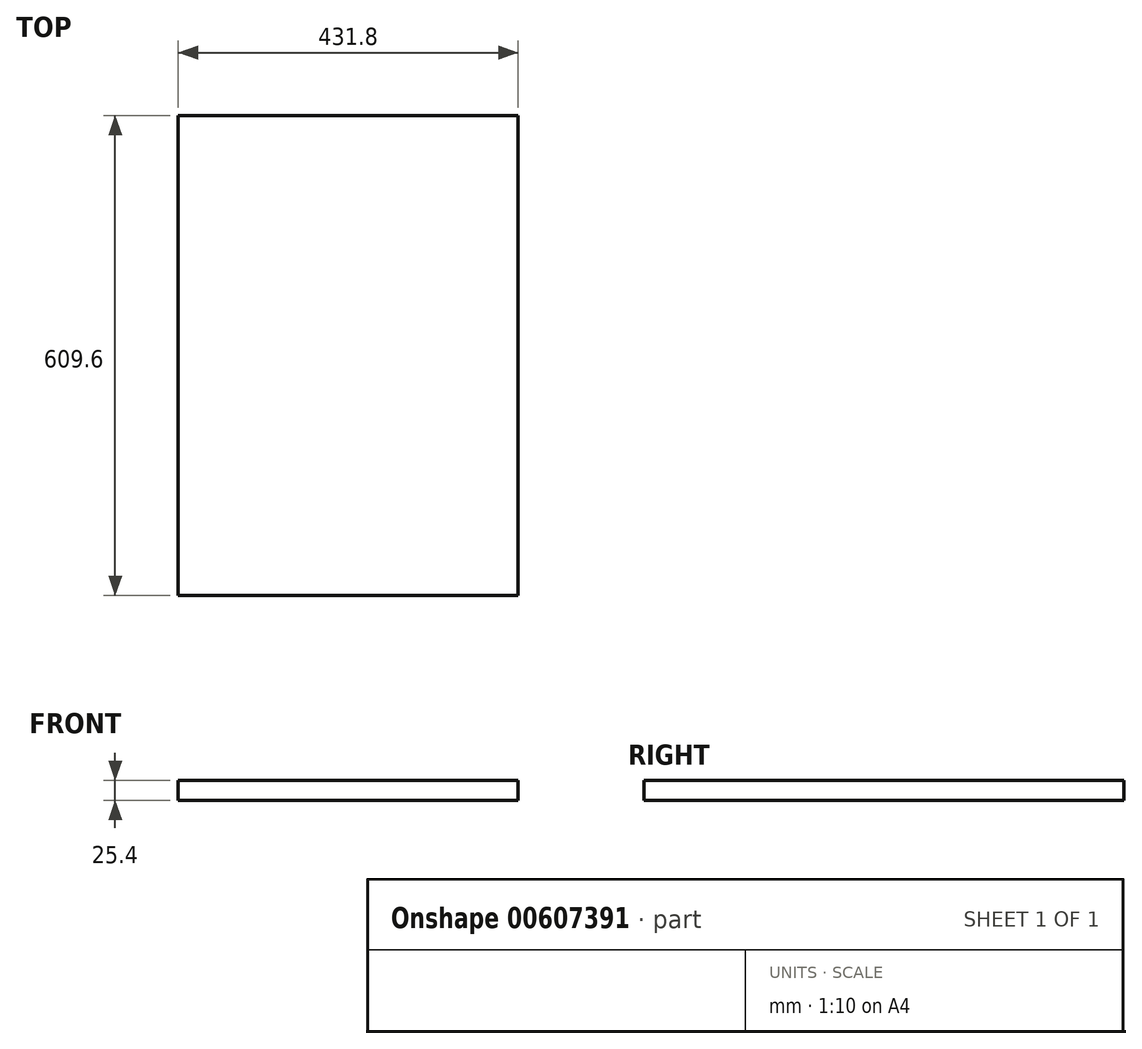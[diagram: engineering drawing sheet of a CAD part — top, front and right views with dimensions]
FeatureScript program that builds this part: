
annotation { "Feature Type Name" : "Feature", "Feature Type Description" : "" }
export const myFeature = defineFeature(function(context is Context, id is Id, definition is map)
    precondition{}
    {
        {
            var Q0;
            Q0=qCreatedBy(makeId("Top.planeOp"),FACE);
            var sketch = newSketch(context, id + "F0", { "sketchPlane" : qUnion([Q0])});
            skLineSegment(sketch, "E0.bottom", {"start": v(215.9, -304.8) * mm, "end": v(-215.9, -304.8) * mm});
            skLineSegment(sketch, "E0.top", {"start": v(215.9, 304.8) * mm, "end": v(-215.9, 304.8) * mm});
            skLineSegment(sketch, "E0.left", {"start": v(215.9, -304.8) * mm, "end": v(215.9, 304.8) * mm});
            skLineSegment(sketch, "E0.right", {"start": v(-215.9, -304.8) * mm, "end": v(-215.9, 304.8) * mm});
            skPoint(sketch, "E0.middle", {"position": v(0, 0) * mm});
            skSolve(sketch);
        }
        {
            var Q0;
            Q0 = qSketchRegion(id + "F0", true);
            extrude(context, id + "F1", {"entities" : qUnion([Q0]), "oppositeDirection" : true, "depth" : 25.4 * mm, "offsetDistance" : 25.4 * mm});
        }
    });
